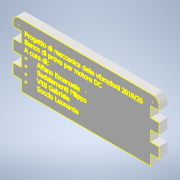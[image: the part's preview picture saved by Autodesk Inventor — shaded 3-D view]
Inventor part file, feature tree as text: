
AUTODESK INVENTOR PART (.ipt)
format: ipt  version: 2020.2 (Build 242310000, 310)  size: 3,406,848 bytes
history: native  units: mm
features: sketch x4, extrude x3, other x2
ambient origin geometry x8: Origin, YZ Plane, XZ Plane, XY Plane, X Axis, Y Axis, Z Axis, Center Point
bodies: Solido1 (feature_tree)
feature tree (9):
  extrude  "Estrusione1"  Depth=70.0mm
  extrude  "Estrusione2"  Depth=30.0mm
  extrude  "Estrusione3"  Depth=4.0mm TaperAngle=0.0deg
  sketch  "Schizzo4"
  sketch  "Schizzo1"
  sketch  "Schizzo2"
  sketch  "Schizzo3"
  other  "Proietta spigoli di taglio1"
  other  "Proietta spigoli di taglio2"
